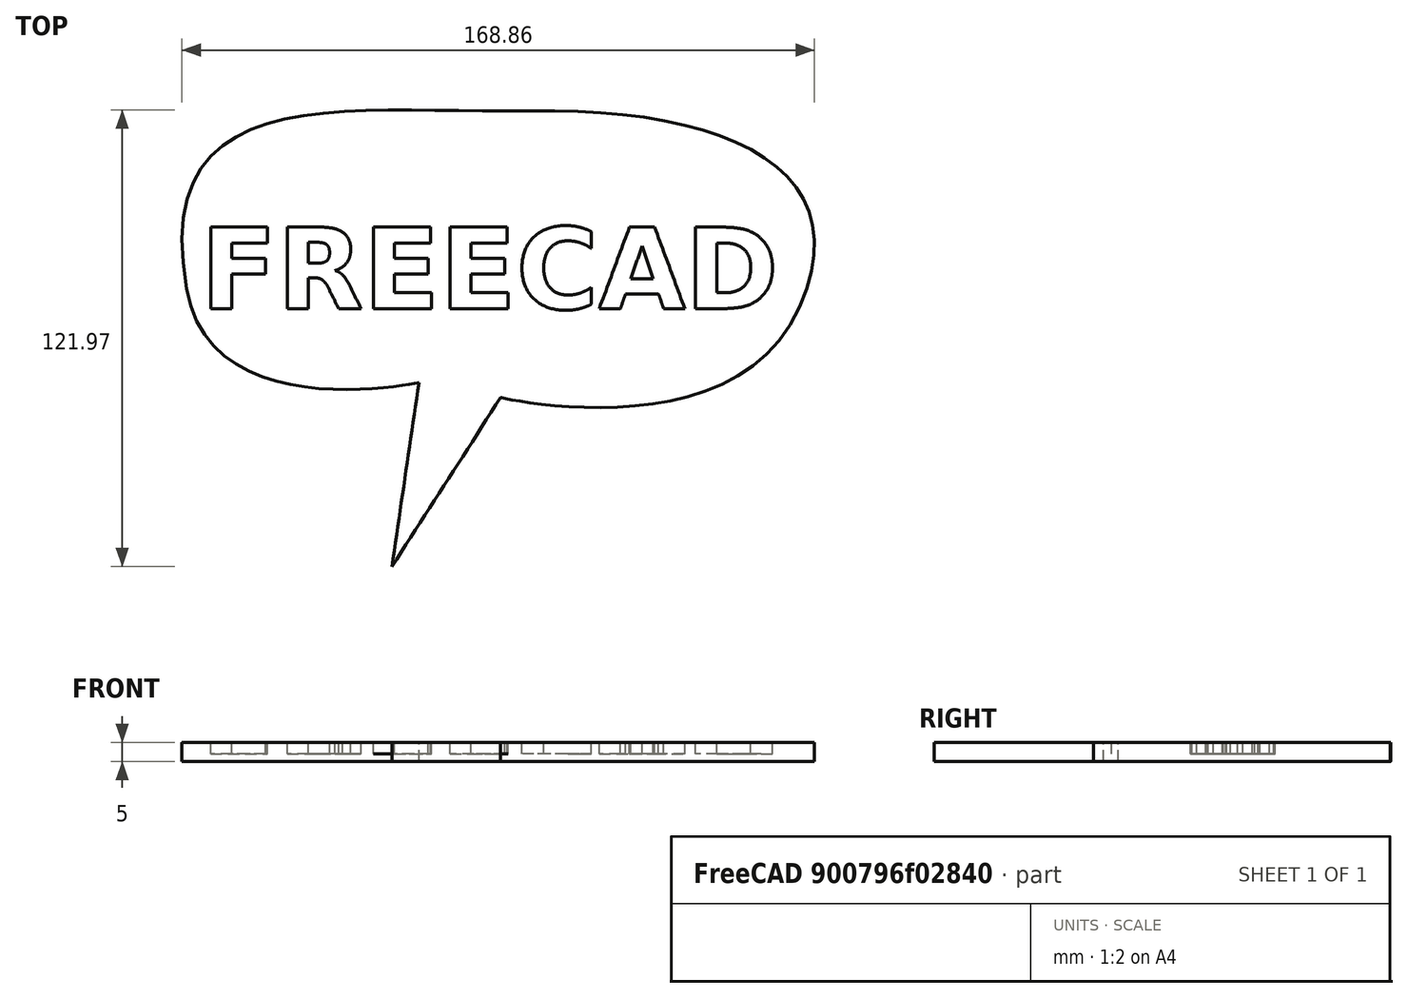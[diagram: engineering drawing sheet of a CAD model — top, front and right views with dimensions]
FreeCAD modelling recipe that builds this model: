
FCSTD DOCUMENT  (FreeCAD 0.16R6706 (Git))
Label: bocadillo
License: All rights reserved
LicenseURL: http://en.wikipedia.org/wiki/All_rights_reserved
objects: Part::Feature×11, Part::Extrusion×11, Part::Cut×4, Part::MultiFuse×1
note: 27 computed .brp shape members not serialized (recipe doc carries the construction recipe); baked Part::Feature solids carry a one-line shape summary decoded from their .brp

FEATURE [Part::Feature] path3361
  shape: bbox 183.7 x 130.9 x 2e-07 mm, 0 faces, 0 solids (baked)
FEATURE [Part::Extrusion] Extrude
  Base = -> path3361
  Dir = (0,0,5)
  Solid = true
FEATURE [Part::Feature] path3418
  shape: bbox 15.18 x 21.81 x 2e-07 mm, 0 faces, 0 solids (baked)
FEATURE [Part::Feature] path3420
  shape: bbox 5.668 x 5.595 x 2e-07 mm, 0 faces, 0 solids (baked)
FEATURE [Part::Feature] path3420001
  shape: bbox 19.69 x 21.81 x 2e-07 mm, 0 faces, 0 solids (baked)
FEATURE [Part::Feature] path3422
  shape: bbox 15.5 x 21.81 x 2e-07 mm, 0 faces, 0 solids (baked)
FEATURE [Part::Feature] path3424
  shape: bbox 15.5 x 21.81 x 2e-07 mm, 0 faces, 0 solids (baked)
FEATURE [Part::Feature] path3426
  shape: bbox 18.55 x 22.63 x 2e-07 mm, 0 faces, 0 solids (baked)
FEATURE [Part::Feature] path3428
  shape: bbox 22.86 x 21.81 x 2e-07 mm, 0 faces, 0 solids (baked)
FEATURE [Part::Feature] path3428001
  shape: bbox 5.974 x 8.677 x 2e-07 mm, 0 faces, 0 solids (baked)
FEATURE [Part::Feature] path3430
  shape: bbox 9.1 x 13.31 x 2e-07 mm, 0 faces, 0 solids (baked)
FEATURE [Part::Feature] path3430001
  shape: bbox 20.52 x 21.81 x 2e-07 mm, 0 faces, 0 solids (baked)
FEATURE [Part::Extrusion] Extrude001
  Base = -> path3418
  Dir = (0,0,3)
  Solid = true
FEATURE [Part::Extrusion] Extrude002
  Base = -> path3420
  Dir = (0,0,3)
  Solid = true
FEATURE [Part::Extrusion] Extrude003
  Base = -> path3420001
  Dir = (0,0,3)
  Solid = true
FEATURE [Part::Extrusion] Extrude004
  Base = -> path3422
  Dir = (0,0,3)
  Solid = true
FEATURE [Part::Extrusion] Extrude005
  Base = -> path3424
  Dir = (0,0,3)
  Solid = true
FEATURE [Part::Extrusion] Extrude006
  Base = -> path3426
  Dir = (0,0,3)
  Solid = true
FEATURE [Part::Extrusion] Extrude007
  Base = -> path3428
  Dir = (0,0,3)
  Solid = true
FEATURE [Part::Extrusion] Extrude008
  Base = -> path3428001
  Dir = (0,0,3)
  Solid = true
FEATURE [Part::Extrusion] Extrude009
  Base = -> path3430
  Dir = (0,0,3)
  Solid = true
FEATURE [Part::Extrusion] Extrude010
  Base = -> path3430001
  Dir = (0,0,3)
  Solid = true
FEATURE [Part::Cut] Cut
  Base = -> Extrude003
  Tool = -> Extrude002
FEATURE [Part::Cut] Cut001
  Base = -> Extrude007
  Tool = -> Extrude008
FEATURE [Part::Cut] Cut002
  Base = -> Extrude010
  Tool = -> Extrude009
FEATURE [Part::MultiFuse] Fusion
  Placement = pos=(0,0,2) rot=(0,0,1;0rad)
  Shapes = -> [Extrude001,Extrude004,Extrude005,Extrude006,Cut002,Cut001,Cut]
FEATURE [Part::Cut] Cut003
  Base = -> Extrude
  Tool = -> Fusion
